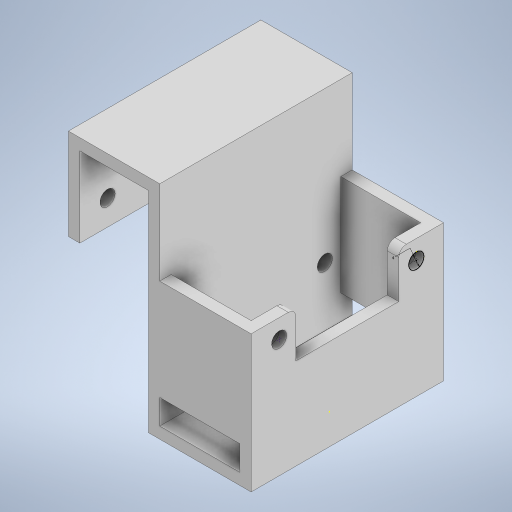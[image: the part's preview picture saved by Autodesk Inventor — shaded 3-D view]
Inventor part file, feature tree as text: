
AUTODESK INVENTOR PART (.ipt)
format: ipt  version: 2023 (Build 270158000, 158)  size: 763,904 bytes
history: native  units: mm
features: sketch x82, extrude x61, fillet x7
ambient origin geometry x8: Origin, YZ Plane, XZ Plane, XY Plane, X Axis, Y Axis, Z Axis, Center Point
bodies: Solid1 (feature_tree)
feature tree (150):
  extrude  "Extrusion1"  Depth=25.0mm
  extrude  "Extrusion2"  Depth=2.0mm
  extrude  "Extrusion3"  Depth=2.0mm
  sketch  "Sketch4"  dims[d8=20.0mm d9=0.0mm d10=4.0mm]
  sketch  "Sketch5"  dims[d11=3.0mm d12=0.0mm d13=5.0mm d14=0.0mm]
  extrude  "Extrusion4"  Depth=4.0mm
  extrude  "Extrusion5"  Depth=3.0mm TaperAngle=0.0deg
  extrude  "Extrusion6"  Depth=4.0mm
  sketch  "Sketch8"  dims[d22=30.0mm d23=0.0mm d24=4.0mm]
  extrude  "Extrusion7"  Depth=2.0mm TaperAngle=0.0deg
  extrude  "Extrusion8"  Depth=4.0mm
  extrude  "Extrusion9"  Depth=8.0mm
  extrude  "Extrusion10"  Depth=8.0mm TaperAngle=0.0deg
  sketch  "Sketch12"  dims[d35=30.0mm d36=0.0mm d37=23.0mm d38=0.0mm]
  sketch  "Sketch13"  dims[d39=4.0mm d40=25.0mm d41=0.0mm]
  extrude  "Extrusion11"  Depth=4.0mm
  extrude  "Extrusion12"  Depth=23.0mm TaperAngle=0.0deg
  extrude  "Extrusion13"  Depth=25.0mm TaperAngle=0.0deg
  sketch  "Sketch16"  dims[d47=25.0mm d48=0.0mm d49=2.0mm]
  sketch  "Sketch17"  dims[d50=25.0mm d51=0.0mm d52=25.0mm d53=0.0mm]
  extrude  "Extrusion14"  Depth=25.0mm TaperAngle=0.0deg
  sketch  "Sketch19"  dims[d57=0.018mm d58=31.0mm d59=0.0mm]
  extrude  "Extrusion15"  Depth=0.3mm
  sketch  "Sketch21"  dims[d62=3.0mm d63=0.0mm d64=3.0mm d65=0.0mm]
  sketch  "Sketch22"  dims[d66=2.0mm d67=2.0mm]
  extrude  "Extrusion16"  Depth=2.0mm
  extrude  "Extrusion17"  Depth=25.0mm TaperAngle=0.0deg
  extrude  "Extrusion18"  Depth=31.0mm TaperAngle=0.0deg
  extrude  "Extrusion19"  Depth=31.0mm TaperAngle=0.0deg
  extrude  "Extrusion20"  Depth=4.0mm
  extrude  "Extrusion21"  Depth=3.0mm TaperAngle=0.0deg
  sketch  "Sketch29"  dims[d95=4.0mm d96=4.0mm]
  extrude  "Extrusion22"  Depth=2.0mm
  sketch  "Sketch31"  dims[d100=3.0mm d101=0.0mm d102=1.0mm]
  sketch  "Sketch32"  dims[d103=3.0mm d104=0.0mm d105=1.0mm d106=0.0mm]
  extrude  "Extrusion23"  Depth=3.0mm TaperAngle=0.0deg
  extrude  "Extrusion24"  Depth=3.0mm TaperAngle=0.0deg
  fillet  "Fillet1"  Radius=25.0mm
  fillet  "Fillet2"  Radius=3.0mm
  sketch  "Sketch33"  dims[d107=1.0mm d108=0.0mm d109=10.0mm d110=0.0mm]
  extrude  "Extrusion25"  Depth=5.0mm TaperAngle=0.0deg
  sketch  "Sketch35"  dims[d114=2.0mm d115=4.0mm]
  extrude  "Extrusion26"  Depth=2.0mm TaperAngle=0.0deg
  sketch  "Sketch37"  dims[d119=5.5mm d120=10.0mm d121=0.0mm]
  extrude  "Extrusion27"  Depth=5.0mm TaperAngle=0.0deg
  extrude  "Extrusion28"  Depth=50.0mm TaperAngle=0.0deg
  sketch  "Sketch40"  dims[d127=70.0mm d128=0.0mm d129=2.0mm]
  extrude  "Extrusion29"  Depth=4.0mm
  extrude  "Extrusion30"  Depth=50.0mm TaperAngle=0.0deg
  extrude  "Extrusion31"  Depth=1.0mm
  sketch  "Sketch44"  dims[d139=20.0mm d140=0.0mm d141=2.0mm d142=10.0mm d143=0.0mm]
  sketch  "Sketch45"  dims[d144=40.0mm d145=0.0mm d146=40.0mm d147=0.0mm]
  extrude  "Extrusion32"  Depth=1.0mm TaperAngle=0.0deg
  sketch  "Sketch47"  dims[d151=21.0mm d152=0.0mm d153=3.0mm]
  extrude  "Extrusion33"  Depth=10.0mm TaperAngle=0.0deg
  extrude  "Extrusion34"  Depth=10.0mm TaperAngle=0.0deg
  extrude  "Extrusion35"  Depth=2.0mm
  extrude  "Extrusion36"  Depth=10.0mm
  extrude  "Extrusion37"  Depth=10.0mm TaperAngle=0.0deg
  extrude  "Extrusion38"  Depth=3.0mm
  extrude  "Extrusion39"  Depth=6.5mm
  extrude  "Extrusion40"  Depth=2.0mm
  extrude  "Extrusion41"  Depth=10.0mm TaperAngle=0.0deg
  extrude  "Extrusion42"  Depth=2.0mm
  sketch  "Sketch58"
  extrude  "Extrusion43"  Depth=3.0mm TaperAngle=0.0deg
  extrude  "Extrusion44"  Depth=2.0mm
  fillet  "Fillet3"  Radius=10.0mm
  extrude  "Extrusion45"  Depth=40.0mm TaperAngle=0.0deg
  sketch  "Sketch62"
  extrude  "Extrusion46"  Depth=3.0mm
  extrude  "Extrusion47"  Depth=3.0mm
  extrude  "Extrusion48"  Depth=21.0mm TaperAngle=0.0deg
  fillet  "Fillet4"  Radius=4.0mm
  fillet  "Fillet5"  Radius=4.0mm
  extrude  "Extrusion49"  Depth=4.0mm
  sketch  "Sketch67"
  sketch  "Sketch68"
  sketch  "Sketch69"
  fillet  "Fillet6"  Radius=4.0mm
  extrude  "Extrusion50"  [1 undecoded]
  extrude  "Extrusion51"  [1 undecoded]
  extrude  "Extrusion52"  [1 undecoded]
  fillet  "Fillet7"  [1 undecoded]
  extrude  "Extrusion53"  [1 undecoded]
  sketch  "Sketch74"
  extrude  "Extrusion54"  [1 undecoded]
  extrude  "Extrusion55"  [1 undecoded]
  extrude  "Extrusion56"  [1 undecoded]
  extrude  "Extrusion57"  [1 undecoded]
  extrude  "Extrusion58"  [1 undecoded]
  extrude  "Extrusion59"  [1 undecoded]
  extrude  "Extrusion60"  [1 undecoded]
  extrude  "Extrusion61"  [1 undecoded]
  sketch  "Sketch1"  dims[d0=20.0mm d1=25.0mm]
  sketch  "Sketch2"  dims[d2=2.0mm d3=0.0mm d4=2.0mm]
  sketch  "Sketch3"  dims[d5=25.0mm d6=0.0mm d7=2.0mm]
  sketch  "Sketch6"  dims[d15=30.0mm d16=0.0mm d17=4.0mm]
  sketch  "Sketch7"  dims[d18=2.0mm d19=0.0mm d20=30.0mm d21=0.0mm]
  sketch  "Sketch9"  dims[d25=2.5mm d26=0.0mm d27=8.0mm]
  sketch  "Sketch10"  dims[d28=8.0mm d29=0.0mm d30=8.0mm d31=0.0mm]
  sketch  "Sketch11"  dims[d32=30.0mm d33=0.0mm d34=4.0mm]
  sketch  "Sketch14"  dims[d42=2.0mm d43=25.0mm d44=0.0mm]
  sketch  "Sketch15"  dims[d45=0.3mm d46=0.3mm]
  sketch  "Sketch18"  dims[d54=3.0mm d55=31.0mm d56=0.0mm]
  sketch  "Sketch20"  dims[d60=4.0mm d61=4.0mm]
  sketch  "Sketch23"  dims[d68=4.0mm d69=3.0mm d70=0.0mm]
  sketch  "Sketch24"  dims[d71=3.0mm d72=0.0mm d73=3.0mm d74=0.0mm d75=25.0mm d76=0.0mm d77=3.0mm d78=0.0mm]
  sketch  "Sketch25"  dims[d79=5.0mm d80=0.0mm d81=5.0mm d82=0.0mm]
  sketch  "Sketch26"  dims[d83=0.0mm d84=0.0mm d85=2.0mm d86=0.0mm]
  sketch  "Sketch27"  dims[d87=5.0mm d88=0.0mm d89=5.0mm d90=0.0mm]
  sketch  "Sketch28"  dims[d91=5.0mm d92=0.0mm d93=50.0mm d94=0.0mm]
  sketch  "Sketch30"  dims[d97=4.0mm d98=50.0mm d99=0.0mm]
  sketch  "Sketch34"  dims[d111=12.0mm d112=10.0mm d113=0.0mm]
  sketch  "Sketch36"  dims[d116=10.0mm d117=0.0mm d118=5.5mm]
  sketch  "Sketch38"  dims[d122=3.0mm d123=3.0mm]
  sketch  "Sketch39"  dims[d124=10.0mm d125=0.0mm d126=6.5mm]
  sketch  "Sketch41"  dims[d130=2.0mm d131=10.0mm d132=0.0mm]
  sketch  "Sketch42"  dims[d133=2.0mm d134=4.0mm]
  sketch  "Sketch43"  dims[d135=19.0mm d136=0.0mm d137=3.0mm d138=0.0mm]
  sketch  "Sketch46"  dims[d148=22.0mm d149=0.0mm d150=3.0mm]
  sketch  "Sketch48"  dims[d154=21.0mm d155=0.0mm d156=21.0mm d157=0.0mm d158=4.0mm d159=4.0mm]
  sketch  "Sketch49"  dims[d160=4.0mm d161=0.0mm d162=4.0mm d163=4.0mm d164=0.0mm]
  sketch  "Sketch50"
  sketch  "Sketch51"
  sketch  "Sketch52"
  sketch  "Sketch53"
  sketch  "Sketch54"
  sketch  "Sketch55"
  sketch  "Sketch56"
  sketch  "Sketch57"
  sketch  "Sketch59"
  sketch  "Sketch60"
  sketch  "Sketch61"
  sketch  "Sketch63"
  sketch  "Sketch64"
  sketch  "Sketch65"
  sketch  "Sketch66"
  sketch  "Sketch70"
  sketch  "Sketch71"
  sketch  "Sketch72"
  sketch  "Sketch73"
  sketch  "Sketch75"
  sketch  "Sketch76"
  sketch  "Sketch77"
  sketch  "Sketch78"
  sketch  "Sketch79"
  sketch  "Sketch80"
  sketch  "Sketch81"
  sketch  "Sketch82"
note: 13 required parameter values undecoded (feature->parameter linkage not recoverable at this tier; creation-order binding heuristic only, values carry confidence <= 0.55)
